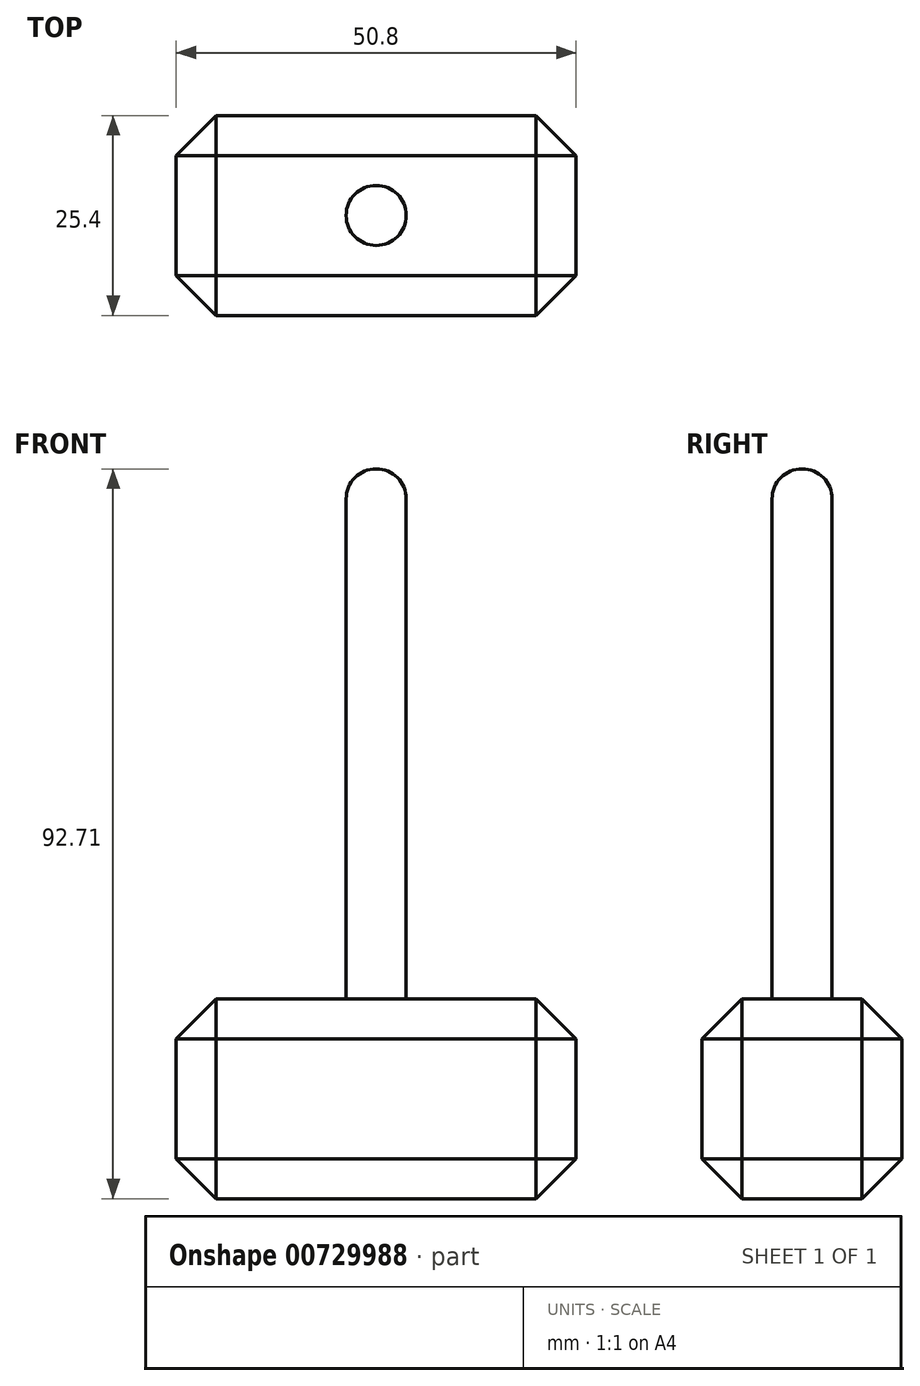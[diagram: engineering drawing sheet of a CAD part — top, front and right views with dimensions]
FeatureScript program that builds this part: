
annotation { "Feature Type Name" : "Feature", "Feature Type Description" : "" }
export const myFeature = defineFeature(function(context is Context, id is Id, definition is map)
    precondition{}
    {
        {
            var Q0;
            Q0=qCreatedBy(makeId("Top.planeOp"),FACE);
            var sketch = newSketch(context, id + "F0", { "sketchPlane" : qUnion([Q0])});
            skLineSegment(sketch, "E0.bottom", {"start": v(25.4, 12.7) * mm, "end": v(-25.4, 12.7) * mm});
            skLineSegment(sketch, "E0.top", {"start": v(25.4, -12.7) * mm, "end": v(-25.4, -12.7) * mm});
            skLineSegment(sketch, "E0.left", {"start": v(25.4, 12.7) * mm, "end": v(25.4, -12.7) * mm});
            skLineSegment(sketch, "E0.right", {"start": v(-25.4, 12.7) * mm, "end": v(-25.4, -12.7) * mm});
            skPoint(sketch, "E0.middle", {"position": v(0, 0) * mm});
            skSolve(sketch);
        }
        {
            var Q0;
            Q0=makeQuery(id+"F0.imprint","IMPRINT",FACE,{"disambiguationData":[TD([[makeQuery(id+"F0.imprint","IMPRINT",EDGE,{"derivedFrom":sQuery(id+"F0.wireOp",EDGE,"E0.bottom")}),1.0]])]});
            extrude(context, id + "F1", {"entities" : qUnion([Q0]), "depth" : 25.4 * mm, "offsetDistance" : 25.4 * mm});
        }
        {
            var Q0;
            Q0=makeQuery(id+"F1.opExtrude","CAP_FACE",FACE,{"disambiguationData":[OSD([sQuery(id+"F0.wireOp",EDGE,"E0.bottom"),sQuery(id+"F0.wireOp",EDGE,"E0.top"),sQuery(id+"F0.wireOp",EDGE,"E0.left"),sQuery(id+"F0.wireOp",EDGE,"E0.right")])],"isStart":false});
            var sketch = newSketch(context, id + "F2", { "sketchPlane" : qUnion([Q0])});
            skCircle(sketch, "E1", {"center": v(0, 0) * mm, "radius": 3.81 * mm});
            skSolve(sketch);
        }
        {
            var Q0;
            Q0=makeQuery(id+"F2.imprint","IMPRINT",FACE,{"disambiguationData":[TD([[makeQuery(id+"F2.imprint","IMPRINT",EDGE,{"derivedFrom":sQuery(id+"F2.wireOp",EDGE,"E1")}),1.0]])]});
            extrude(context, id + "F3", {"entities" : qUnion([Q0]), "operationType" : NewBodyOperationType.ADD, "depth" : 63.5 * mm, "offsetDistance" : 25.4 * mm});
        }
        {
            var Q0;
            Q0=makeQuery(id+"F3.opExtrude","CAP_FACE",FACE,{"disambiguationData":[OSD([sQuery(id+"F2.wireOp",EDGE,"E1")])],"isStart":false});
            var sketch = newSketch(context, id + "F4", { "sketchPlane" : qUnion([Q0])});
            skArc(sketch, "E2", {"start": v(0, -3.81) * mm, "mid": v(3.81, 0) * mm, "end": v(0, 3.81) * mm});
            skLineSegment(sketch, "E3", {"start": v(0, 3.81) * mm, "end": v(0, -3.81) * mm});
            skSolve(sketch);
        }
        {
            var Q0;
            Q0=makeQuery(id+"F4.imprint","IMPRINT",FACE,{"disambiguationData":[TD([[makeQuery(id+"F4.imprint","IMPRINT",EDGE,{"derivedFrom":sQuery(id+"F4.wireOp",EDGE,"E2")}),1.0]])]});
            var Q1;
            Q1=sQuery(id+"F4.wireOp",EDGE,"E3");
            revolve(context, id + "F5", {"operationType" : NewBodyOperationType.ADD, "surfaceOperationType" : NewSurfaceOperationType.NEW, "entities" : qUnion([Q0]), "axis" : qUnion([Q1]), "revolveType" : RevolveType.FULL});
        }
        {
            var Q0;
            Q0=makeQuery(id+"F1.opExtrude","CAP_EDGE",EDGE,{"disambiguationData":[OSD([sQuery(id+"F0.wireOp",EDGE,"E0.right")])],"isStart":false});
            var Q1;
            Q1=makeQuery(id+"F1.opExtrude","CAP_EDGE",EDGE,{"disambiguationData":[OSD([sQuery(id+"F0.wireOp",EDGE,"E0.left")])],"isStart":false});
            var Q2;
            Q2=makeQuery(id+"F1.opExtrude","CAP_EDGE",EDGE,{"disambiguationData":[OSD([sQuery(id+"F0.wireOp",EDGE,"E0.top")])],"isStart":false});
            var Q3;
            Q3=makeQuery(id+"F1.opExtrude","CAP_EDGE",EDGE,{"disambiguationData":[OSD([sQuery(id+"F0.wireOp",EDGE,"E0.bottom")])],"isStart":false});
            var Q4;
            Q4=makeQuery(id+"F1.opExtrude","CAP_EDGE",EDGE,{"disambiguationData":[OSD([sQuery(id+"F0.wireOp",EDGE,"E0.top")])],"isStart":true});
            var Q5;
            Q5=makeQuery(id+"F1.opExtrude","CAP_EDGE",EDGE,{"disambiguationData":[OSD([sQuery(id+"F0.wireOp",EDGE,"E0.bottom")])],"isStart":true});
            var Q6;
            Q6=makeQuery(id+"F1.opExtrude","CAP_EDGE",EDGE,{"disambiguationData":[OSD([sQuery(id+"F0.wireOp",EDGE,"E0.right")])],"isStart":true});
            var Q7;
            Q7=makeQuery(id+"F1.opExtrude","CAP_EDGE",EDGE,{"disambiguationData":[OSD([sQuery(id+"F0.wireOp",EDGE,"E0.left")])],"isStart":true});
            var Q8;
            Q8=makeQuery(id+"F1.opExtrude","SWEPT_EDGE",EDGE,{"disambiguationData":[OSD([sQuery(id+"F0.wireOp",EDGE,"E0.top"),sQuery(id+"F0.wireOp",EDGE,"E0.left")])]});
            var Q9;
            Q9=makeQuery(id+"F1.opExtrude","SWEPT_EDGE",EDGE,{"disambiguationData":[OSD([sQuery(id+"F0.wireOp",EDGE,"E0.bottom"),sQuery(id+"F0.wireOp",EDGE,"E0.left")])]});
            var Q10;
            Q10=makeQuery(id+"F1.opExtrude","SWEPT_EDGE",EDGE,{"disambiguationData":[OSD([sQuery(id+"F0.wireOp",EDGE,"E0.bottom"),sQuery(id+"F0.wireOp",EDGE,"E0.right")])]});
            var Q11;
            Q11=makeQuery(id+"F1.opExtrude","SWEPT_EDGE",EDGE,{"disambiguationData":[OSD([sQuery(id+"F0.wireOp",EDGE,"E0.top"),sQuery(id+"F0.wireOp",EDGE,"E0.right")])]});
            chamfer(context, id + "F6", {"entities" : qUnion([Q0, Q1, Q2, Q3, Q4, Q5, Q6, Q7, Q8, Q9, Q10, Q11]), "width" : 5.08 * mm, "tangentPropagation" : true});
        }
    });
